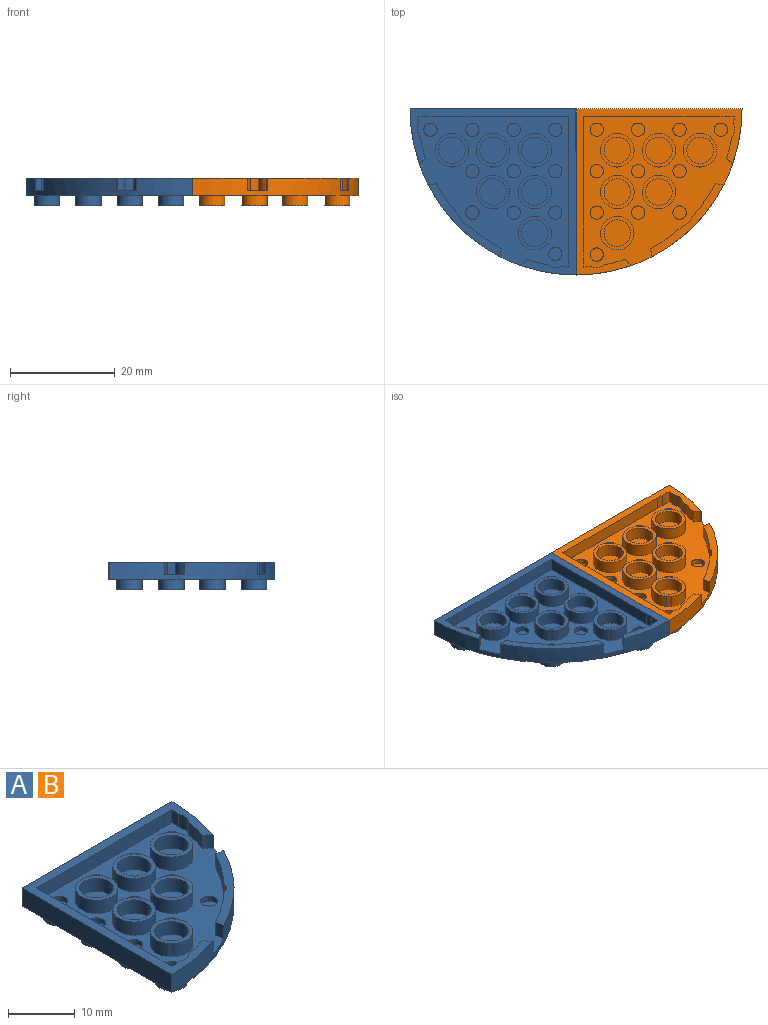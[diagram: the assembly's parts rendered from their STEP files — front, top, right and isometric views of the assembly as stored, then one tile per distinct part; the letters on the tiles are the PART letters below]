
ASSEMBLY  parts=2 mates=1
PART A: 101 faces, bbox 31.8x31.8x5.3 mm
  f0: cylinder r=2.54mm len=2.41mm, axis (0,0,-1), area 3.8mm2, adj f3,f4,f8,f9
  f1: cylinder r=2.54mm len=2.41mm, axis (0,0,-1), area 2.1mm2, adj f6,f7,f9,f12
  f2: plane 31.75x31.75mm, normal (0,0,-1), area 590.5mm2, adj f8,f20,f28,f39,f40,f46,f52,f59
  f3: cylinder r=30.29mm len=6.33mm, axis (0,0,-1), area 18.8mm2, adj f0,f4,f9,f78
  f4: plane 14.1x14.1mm, normal (0,0,1), area 27mm2, adj f0,f3,f8,f78,f79,f91
  f5: plane 31.75x31.75mm, normal (0,0,1), area 116.9mm2, adj f8,f10,f14,f19,f20,f47,f49,f50
  f6: cylinder r=3.2mm len=6.4mm, axis (0,0,-1), area 34.2mm2, adj f1,f7,f9,f48
  f7: plane 6.4x6.4mm, normal (0,0,1), area 11.8mm2, adj f1,f6,f11,f12,f48
  f8: cylinder r=31.75mm len=31.75mm, axis (0,0,-1), area 144.6mm2, adj f0,f2,f4,f5,f9,f14,f20,f52
  f9: plane 28.91x28.91mm, normal (0,0,1), area 399.3mm2, adj f0,f1,f3,f6,f8,f10,f12,f14
  f10: cylinder r=30.29mm len=3.99mm, axis (0,0,-1), area 10mm2, adj f5,f9,f14,f53
  f11: cylinder r=2.54mm len=5.08mm, axis (0,0,-1), area 38.5mm2, adj f7,f13
  f12: cylinder r=3.2mm len=3.75mm, axis (0,0,-1), area 9.7mm2, adj f1,f7,f9,f48
  f13: plane 5.08x5.08mm, normal (0,0,1), area 20.3mm2, adj f11
  f14: cylinder r=2.54mm len=2.41mm, axis (0,0,-1), area 3.8mm2, adj f5,f8,f9,f10
  f15: plane 5.08x5.08mm, normal (0,0,1), area 20.3mm2, adj f16
  f16: cylinder r=2.54mm len=5.08mm, axis (0,0,-1), area 38.5mm2, adj f15,f17
  f17: plane 6.4x6.4mm, normal (0,0,1), area 11.9mm2, adj f16,f18
  f18: cylinder r=3.2mm len=6.4mm, axis (0,0,-1), area 48.5mm2, adj f9,f17
  f19: plane 25.67x2.41mm, normal (1,0,0), area 61.9mm2, adj f5,f9,f50,f95
  f20: plane 31.75x3.3mm, normal (-1,0,0), area 104.8mm2, adj f2,f5,f8,f52
  f21: plane 2.54x2.54mm, normal (0,0,1), area 5.1mm2, adj f27
  f22: plane 4.83x4.83mm, normal (0,0,-1), area 18.3mm2, adj f28
  f23: plane 6.4x6.4mm, normal (0,0,1), area 11.9mm2, adj f24,f26
  f24: cylinder r=2.54mm len=5.08mm, axis (0,0,-1), area 38.5mm2, adj f23,f25
  f25: plane 5.08x5.08mm, normal (0,0,1), area 20.3mm2, adj f24
  f26: cylinder r=3.2mm len=6.4mm, axis (0,0,-1), area 48.5mm2, adj f9,f23
  f27: cylinder r=1.27mm len=2.54mm, axis (0,0,-1), area 7.1mm2, adj f9,f21
  f28: cylinder r=2.41mm len=4.83mm, axis (0,0,1), area 29.7mm2, adj f2,f22
  f29: plane 2.54x2.54mm, normal (0,0,1), area 5.1mm2, adj f37
  f30: plane 2.54x2.54mm, normal (0,0,1), area 5.1mm2, adj f38
  f31: plane 4.83x4.83mm, normal (0,0,-1), area 18.3mm2, adj f39
  f32: plane 4.83x4.83mm, normal (0,0,-1), area 18.3mm2, adj f40
  f33: plane 6.4x6.4mm, normal (0,0,1), area 11.9mm2, adj f34,f36
  f34: cylinder r=2.54mm len=5.08mm, axis (0,0,-1), area 38.5mm2, adj f33,f35
  f35: plane 5.08x5.08mm, normal (0,0,1), area 20.3mm2, adj f34
  f36: cylinder r=3.2mm len=6.4mm, axis (0,0,-1), area 48.5mm2, adj f9,f33
  f37: cylinder r=1.27mm len=2.54mm, axis (0,0,-1), area 7.1mm2, adj f9,f29
  f38: cylinder r=1.27mm len=2.54mm, axis (0,0,-1), area 7.1mm2, adj f9,f30
  f39: cylinder r=2.41mm len=4.83mm, axis (0,0,1), area 29.7mm2, adj f2,f31
  f40: cylinder r=2.41mm len=4.83mm, axis (0,0,1), area 29.7mm2, adj f2,f32
  f41: plane 5.08x5.08mm, normal (0,0,1), area 20.3mm2, adj f44
  f42: plane 6.4x6.4mm, normal (0,0,1), area 11.8mm2, adj f43,f44,f84
  f43: cylinder r=3.2mm len=6.4mm, axis (0,0,-1), area 45.5mm2, adj f9,f42,f84
  f44: cylinder r=2.54mm len=5.08mm, axis (0,0,-1), area 38.5mm2, adj f41,f42
  f45: plane 4.83x4.83mm, normal (0,0,-1), area 18.3mm2, adj f46
  f46: cylinder r=2.41mm len=4.83mm, axis (0,0,1), area 29.7mm2, adj f2,f45
  f47: cylinder r=2.54mm len=2.41mm, axis (0,0,-1), area 3mm2, adj f5,f9,f50,f51
  f48: cylinder r=2.54mm len=2.41mm, axis (0,0,-1), area 2.6mm2, adj f6,f7,f9,f12
  f49: cylinder r=30.29mm len=2.41mm, axis (0,0,-1), area 3.6mm2, adj f5,f9,f51,f53
  f50: plane 25.67x2.41mm, normal (0,-1,0), area 61.9mm2, adj f5,f9,f19,f47
  f51: plane 2.41x1.85mm, normal (0,-1,0), area 4.5mm2, adj f5,f9,f47,f49
  f52: plane 31.75x3.3mm, normal (0,1,0), area 104.8mm2, adj f2,f5,f8,f20
  f53: cylinder r=2.54mm len=2.54mm, axis (0,0,-1), area 6.5mm2, adj f5,f9,f10,f49
  f54: cylinder r=1.27mm len=2.54mm, axis (0,0,-1), area 7.1mm2, adj f9,f55
  f55: plane 2.54x2.54mm, normal (0,0,1), area 5.1mm2, adj f54
  f56: plane 2.54x2.54mm, normal (0,0,1), area 5.1mm2, adj f58
  f57: plane 4.83x4.83mm, normal (0,0,-1), area 18.3mm2, adj f59
  f58: cylinder r=1.27mm len=2.54mm, axis (0,0,-1), area 7.1mm2, adj f9,f56
  f59: cylinder r=2.41mm len=4.83mm, axis (0,0,1), area 29.7mm2, adj f2,f57
  f60: plane 2.54x2.54mm, normal (0,0,1), area 5.1mm2, adj f64
  f61: plane 2.54x2.54mm, normal (0,0,1), area 5.1mm2, adj f65
  f62: plane 4.83x4.83mm, normal (0,0,-1), area 18.3mm2, adj f66
  f63: plane 4.83x4.83mm, normal (0,0,-1), area 18.3mm2, adj f67
  f64: cylinder r=1.27mm len=2.54mm, axis (0,0,-1), area 7.1mm2, adj f9,f60
  f65: cylinder r=1.27mm len=2.54mm, axis (0,0,-1), area 7.1mm2, adj f9,f61
  f66: cylinder r=2.41mm len=4.83mm, axis (0,0,1), area 29.7mm2, adj f2,f62
  f67: cylinder r=2.41mm len=4.83mm, axis (0,0,1), area 29.7mm2, adj f2,f63
  f68: plane 4.83x4.83mm, normal (0,0,-1), area 18.3mm2, adj f70
  f69: plane 2.54x2.54mm, normal (0,0,1), area 5.1mm2, adj f71
  f70: cylinder r=2.41mm len=4.83mm, axis (0,0,1), area 29.7mm2, adj f2,f68
  f71: cylinder r=1.27mm len=2.54mm, axis (0,0,-1), area 7.1mm2, adj f9,f69
  f72: plane 5.08x5.08mm, normal (0,0,1), area 20.3mm2, adj f73
  f73: cylinder r=2.54mm len=5.08mm, axis (0,0,-1), area 38.5mm2, adj f72,f74
  f74: plane 6.4x6.4mm, normal (0,0,1), area 11.8mm2, adj f73,f75,f88,f89,f94
  f75: cylinder r=3.2mm len=6.4mm, axis (0,0,-1), area 34.2mm2, adj f9,f74,f88,f94
  f76: plane 4.83x4.83mm, normal (0,0,-1), area 18.3mm2, adj f77
  f77: cylinder r=2.41mm len=4.83mm, axis (0,0,1), area 29.7mm2, adj f2,f76
  f78: cylinder r=2.54mm len=2.41mm, axis (0,0,-1), area 6.3mm2, adj f3,f4,f9,f79
  f79: cylinder r=30.29mm len=6.28mm, axis (0,0,-1), area 18.6mm2, adj f4,f9,f78,f91
  f80: cylinder r=1.27mm len=2.54mm, axis (0,0,-1), area 7.1mm2, adj f9,f83
  f81: plane 4.83x4.83mm, normal (0,0,-1), area 18.3mm2, adj f82
  f82: cylinder r=2.41mm len=4.83mm, axis (0,0,1), area 29.7mm2, adj f2,f81
  f83: plane 2.54x2.54mm, normal (0,0,1), area 5.1mm2, adj f80
  f84: cylinder r=2.54mm len=2.41mm, axis (0,0,-1), area 3mm2, adj f9,f42,f43
  f85: cylinder r=1.27mm len=2.54mm, axis (0,0,-1), area 7.1mm2, adj f9,f86
  f86: plane 2.54x2.54mm, normal (0,0,1), area 5.1mm2, adj f85
  f87: cylinder r=2.54mm len=2.41mm, axis (0,0,-1), area 3.8mm2, adj f5,f8,f9,f90
  f88: cylinder r=2.54mm len=2.41mm, axis (0,0,-1), area 2.1mm2, adj f9,f74,f75,f89
  f89: cylinder r=3.2mm len=3.75mm, axis (0,0,-1), area 9.7mm2, adj f9,f74,f88,f94
  f90: cylinder r=30.29mm len=3.99mm, axis (0,0,-1), area 10mm2, adj f5,f9,f87,f98
  f91: cylinder r=2.54mm len=2.41mm, axis (0,0,-1), area 3.8mm2, adj f4,f8,f9,f79
  f92: plane 4.83x4.83mm, normal (0,0,-1), area 18.3mm2, adj f93
  f93: cylinder r=2.41mm len=4.83mm, axis (0,0,1), area 29.7mm2, adj f2,f92
  f94: cylinder r=2.54mm len=2.41mm, axis (0,0,-1), area 2.6mm2, adj f9,f74,f75,f89
  f95: cylinder r=2.54mm len=2.41mm, axis (0,0,-1), area 3mm2, adj f5,f9,f19,f96
  f96: plane 2.41x1.85mm, normal (1,0,0), area 4.5mm2, adj f5,f9,f95,f97
  f97: cylinder r=30.29mm len=2.41mm, axis (0,0,-1), area 3.6mm2, adj f5,f9,f96,f98
  f98: cylinder r=2.54mm len=2.54mm, axis (0,0,-1), area 6.5mm2, adj f5,f9,f90,f97
  f99: cylinder r=1.27mm len=2.54mm, axis (0,0,-1), area 7.1mm2, adj f9,f100
  f100: plane 2.54x2.54mm, normal (0,0,1), area 5.1mm2, adj f99
PART B: same geometry as A
PLACE A rot(axis=(0,0,-1),90deg) t=(-31.75,0,0)mm
PLACE B at identity
MATE fastened A.f52 <-> B.f20  axis (1,0,0) through (-15.88,0,1.65)mm
